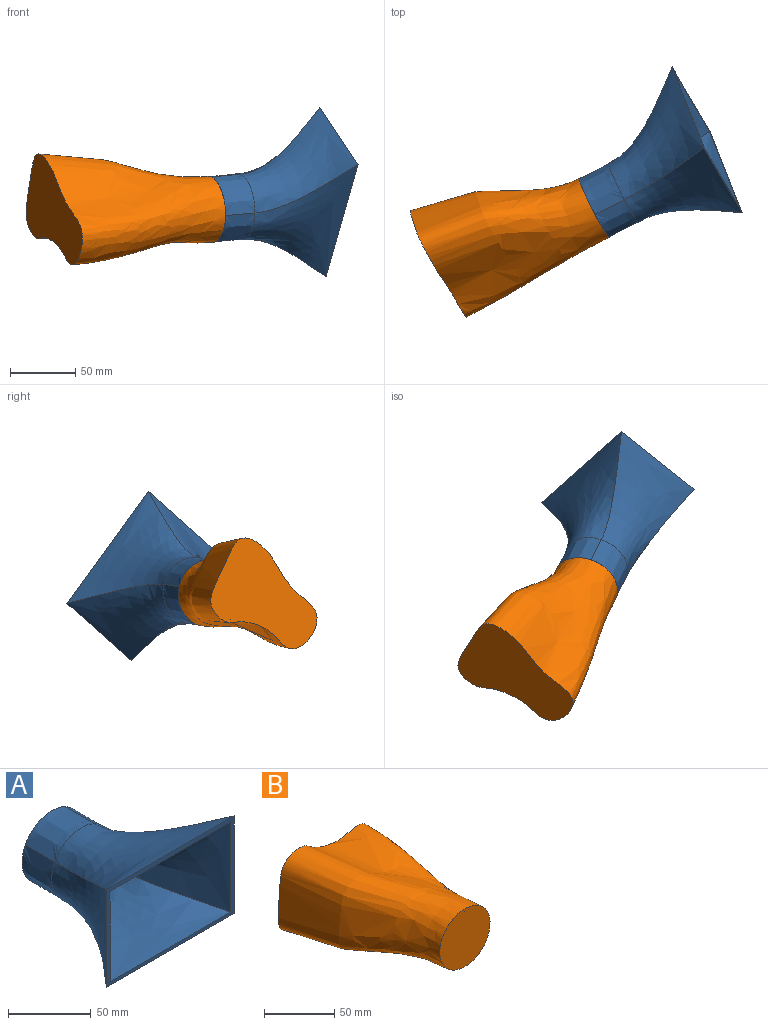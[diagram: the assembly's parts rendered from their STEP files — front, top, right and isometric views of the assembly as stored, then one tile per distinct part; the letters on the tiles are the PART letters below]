
ASSEMBLY  parts=2 mates=1
PART A: 18 faces, bbox 116.5x106.7x78.3 mm
  f0: plane 110x73.25mm, normal (0,-1,0), area 992.8mm2, adj f1,f2,f3,f4,f5,f6,f7,f8
  f1: bspline ~76.2x72.51mm, area 4357.7mm2, adj f0,f2,f4,f10
  f2: bspline ~110.35x76.2mm, area 5271.9mm2, adj f0,f1,f3,f9
  f3: bspline ~76.2x73.23mm, area 4315.9mm2, adj f0,f2,f4,f12
  f4: bspline ~111.45x76.2mm, area 4960.1mm2, adj f0,f1,f3,f11
  f5: offset ~81.28x77.58mm, area 3950.8mm2, adj f0,f6,f8,f15
  f6: offset ~114.71x81.28mm, area 4847.6mm2, adj f0,f5,f7,f14
  f7: offset ~81.28x77.83mm, area 3900.5mm2, adj f0,f6,f8,f17
  f8: offset ~115.07x81.28mm, area 4564.1mm2, adj f0,f5,f7,f16
  f9: extruded ~34.1x25.4mm, area 1013.3mm2, adj f2,f10,f12,f13
  f10: extruded ~34.1x25.4mm, area 1013.3mm2, adj f1,f9,f11,f13
  f11: extruded ~34.1x25.4mm, area 1013.3mm2, adj f4,f10,f12,f13
  f12: extruded ~34.1x25.4mm, area 1013.3mm2, adj f3,f9,f11,f13
  f13: plane 50.88x50.88mm, normal (0,1,0), area 385.1mm2, adj f9,f10,f11,f12,f14,f15,f16,f17
  f14: extruded ~30.69x25.4mm, area 912mm2, adj f6,f13,f15,f17
  f15: extruded ~30.69x25.4mm, area 912mm2, adj f5,f13,f14,f16
  f16: extruded ~30.69x25.4mm, area 912mm2, adj f8,f13,f15,f17
  f17: extruded ~30.69x25.4mm, area 912mm2, adj f7,f13,f14,f16
PART B: 4 faces, bbox 1574.4x1261.9x1640.4 mm
  f0: plane 240.6x240.6mm, normal (0,-1,0), area 385.1mm2, adj f2,f3
  f1: plane 1230.21x1200.6mm, normal (0,1,0), area 675.6mm2, adj f2,f3
  f2: bspline ~127x95.41mm, area 27933.8mm2, adj f0,f1
  f3: offset ~510.18x444.6mm, area 99099mm2, adj f0,f1
PLACE A rot(axis=(-0.45,0.23,0.86),122.3deg) t=(84.19,38.27,20.46)mm
PLACE B rot(axis=(-0.84,0.5,0.2),160.9deg) t=(-51,-31.07,8.59)mm
MATE revolute A.f13 <-> B.f0  axis (0.89,0.46,0.08) through (61.66,26.71,18.48)mm
